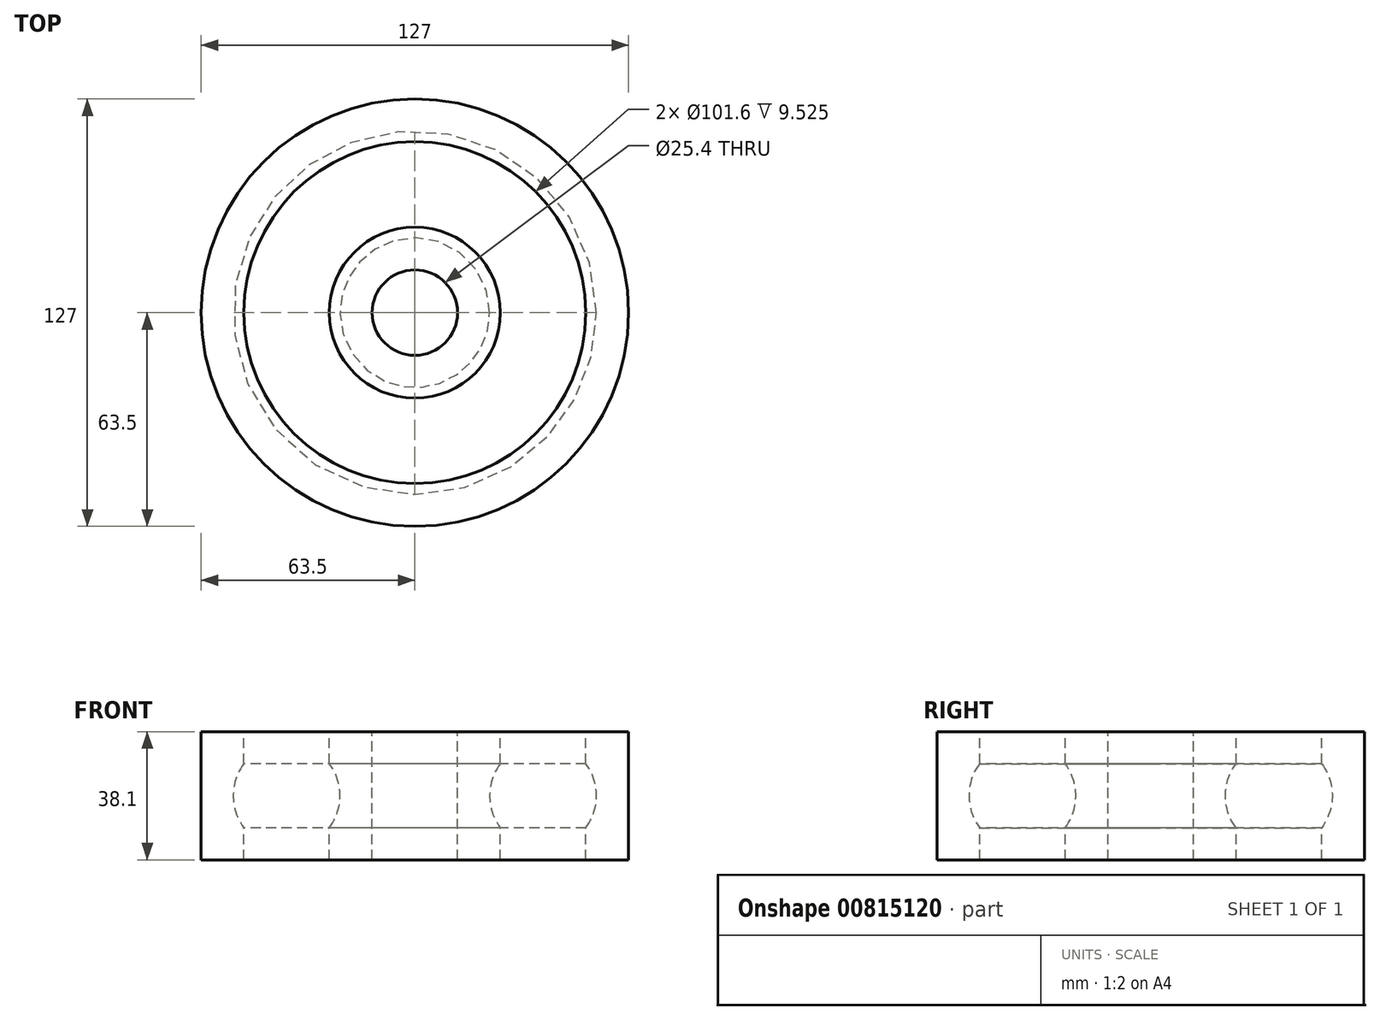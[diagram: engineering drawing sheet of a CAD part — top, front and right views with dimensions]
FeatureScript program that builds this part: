
annotation { "Feature Type Name" : "Feature", "Feature Type Description" : "" }
export const myFeature = defineFeature(function(context is Context, id is Id, definition is map)
    precondition{}
    {
        {
            var Q0;
            Q0=qCreatedBy(makeId("Front.planeOp"),FACE);
            var sketch = newSketch(context, id + "F0", { "sketchPlane" : qUnion([Q0])});
            skLineSegment(sketch, "E0", {"start": v(0, 19.05) * mm, "end": v(0, -19.05) * mm, "construction": true});
            skLineSegment(sketch, "E1", {"start": v(12.7, 19.05) * mm, "end": v(12.7, -19.05) * mm});
            skLineSegment(sketch, "E2", {"start": v(12.7, -19.05) * mm, "end": v(25.4, -19.05) * mm});
            skLineSegment(sketch, "E3", {"start": v(25.4, -19.05) * mm, "end": v(25.4, 19.05) * mm});
            skLineSegment(sketch, "E4", {"start": v(25.4, 19.05) * mm, "end": v(12.7, 19.05) * mm});
            skCircle(sketch, "E5", {"center": v(38.1, 0) * mm, "radius": 15.88 * mm});
            skLineSegment(sketch, "E6.bottom", {"start": v(50.8, 19.05) * mm, "end": v(63.5, 19.05) * mm});
            skLineSegment(sketch, "E6.top", {"start": v(50.8, -19.05) * mm, "end": v(63.5, -19.05) * mm});
            skLineSegment(sketch, "E6.left", {"start": v(50.8, 19.05) * mm, "end": v(50.8, -19.05) * mm});
            skLineSegment(sketch, "E6.right", {"start": v(63.5, 19.05) * mm, "end": v(63.5, -19.05) * mm});
            skLineSegment(sketch, "E7", {"start": v(22.22, 0) * mm, "end": v(53.97, 0) * mm});
            skLineSegment(sketch, "E8", {"start": v(12.7, 0) * mm, "end": v(22.22, 0) * mm, "construction": true});
            skLineSegment(sketch, "E9", {"start": v(53.97, 0) * mm, "end": v(63.5, 0) * mm, "construction": true});
            skSolve(sketch);
        }
        {
            var Q0;
            Q0=makeQuery(id+"F0.imprint","IMPRINT",FACE,{"disambiguationData":[TD([[makeQuery(id+"F0.imprint","IMPRINT",EDGE,{"derivedFrom":sQuery(id+"F0.wireOp",EDGE,"E1")}),1.0]])]});
            var Q1;
            {var subQ1=sQuery(id+"F0.wireOp",EDGE,"E6.bottom");Q1=makeQuery(id+"F0.imprint","IMPRINT",FACE,{"disambiguationData":[TD([[makeQuery(id+"F0.imprint","IMPRINT",EDGE,{"derivedFrom":subQ1}),-1.0]])]});}
            var Q2;
            Q2=sQuery(id+"F0.wireOp",EDGE,"E0");
            revolve(context, id + "F1", {"entities" : qUnion([Q0, Q1]), "axis" : qUnion([Q2]), "revolveType" : RevolveType.FULL});
        }
    });
